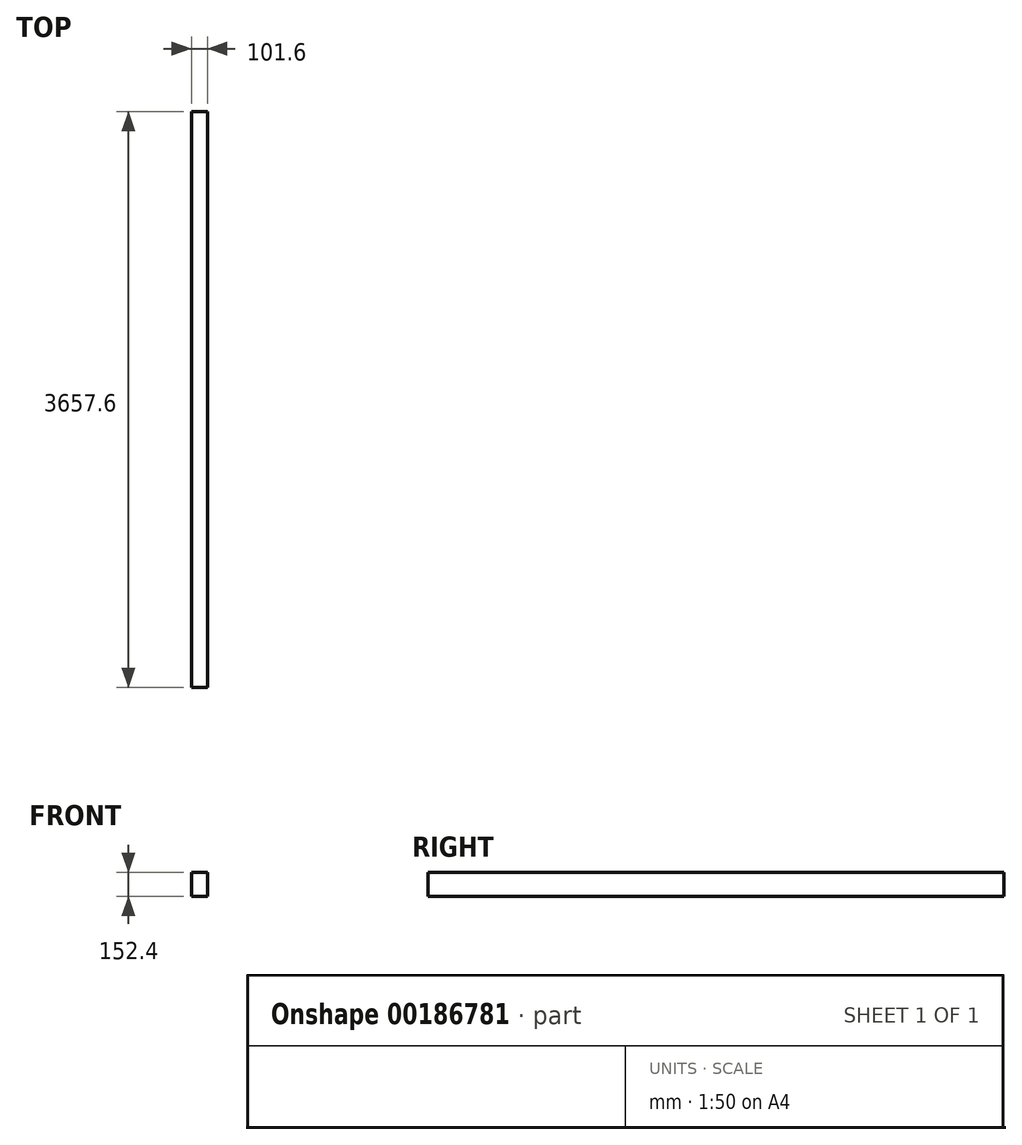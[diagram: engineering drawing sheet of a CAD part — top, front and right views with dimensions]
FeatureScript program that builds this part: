
annotation { "Feature Type Name" : "Feature", "Feature Type Description" : "" }
export const myFeature = defineFeature(function(context is Context, id is Id, definition is map)
    precondition{}
    {
        {
            var Q0;
            Q0=qCreatedBy(makeId("Front.planeOp"),FACE);
            var sketch = newSketch(context, id + "F0", { "sketchPlane" : qUnion([Q0])});
            skLineSegment(sketch, "E0.bottom", {"start": v(-50.8, 76.2) * mm, "end": v(50.8, 76.2) * mm});
            skLineSegment(sketch, "E0.top", {"start": v(-50.8, -76.2) * mm, "end": v(50.8, -76.2) * mm});
            skLineSegment(sketch, "E0.left", {"start": v(-50.8, 76.2) * mm, "end": v(-50.8, -76.2) * mm});
            skLineSegment(sketch, "E0.right", {"start": v(50.8, 76.2) * mm, "end": v(50.8, -76.2) * mm});
            skPoint(sketch, "E0.middle", {"position": v(0, 0) * mm});
            skSolve(sketch);
        }
        {
            var Q0;
            Q0 = qSketchRegion(id + "F0", true);
            extrude(context, id + "F1", {"entities" : qUnion([Q0]), "depth" : 3657.6 * mm});
        }
    });
